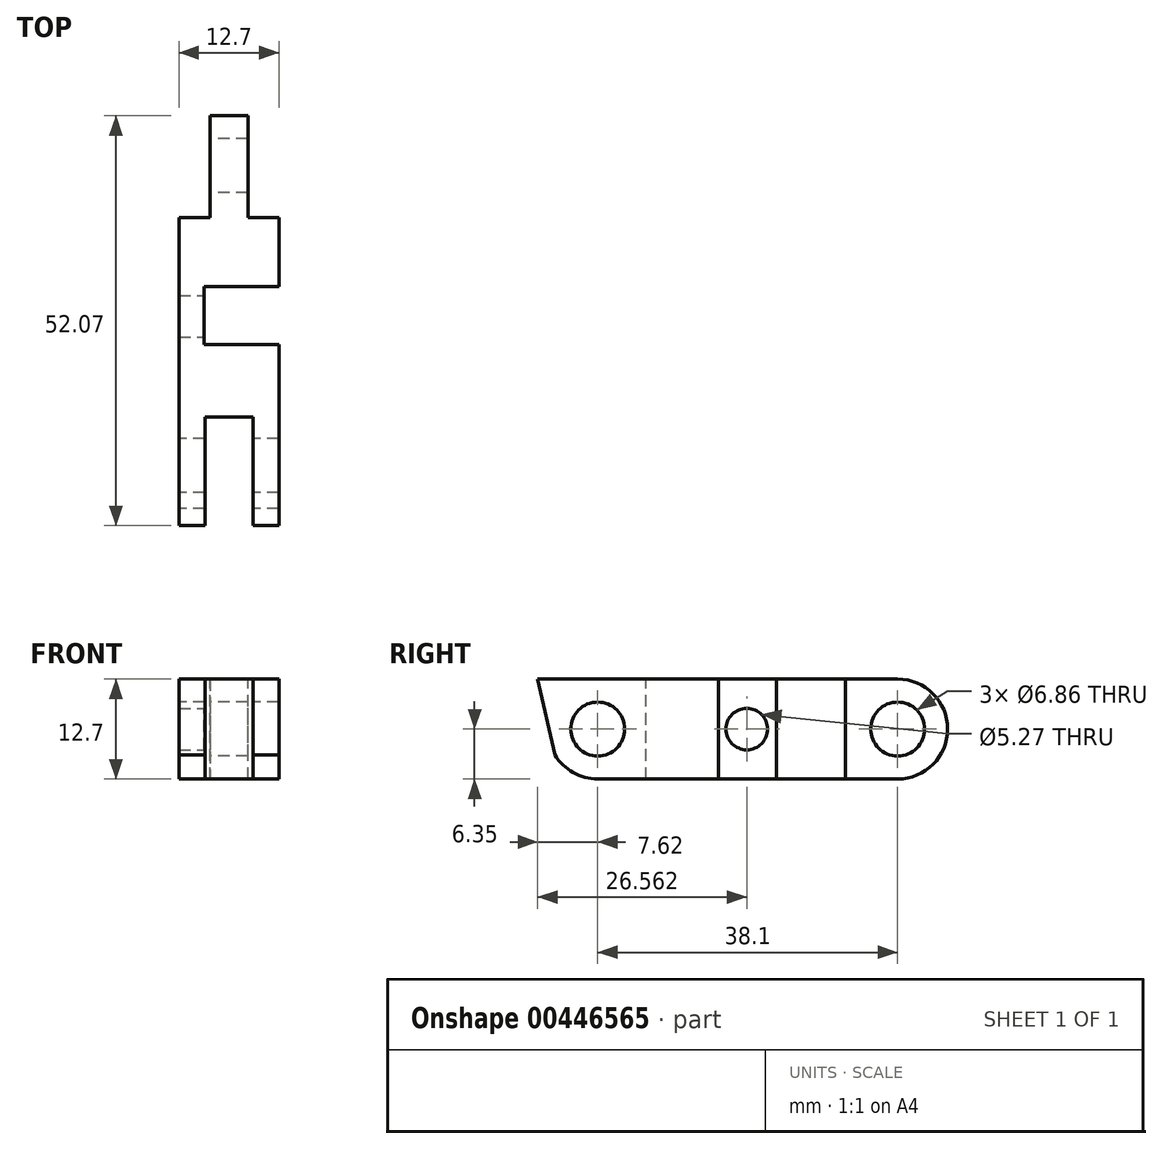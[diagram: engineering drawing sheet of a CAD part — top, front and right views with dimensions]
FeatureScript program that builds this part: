
annotation { "Feature Type Name" : "Feature", "Feature Type Description" : "" }
export const myFeature = defineFeature(function(context is Context, id is Id, definition is map)
    precondition{}
    {
        {
            var Q0;
            Q0=qCreatedBy(makeId("Right.planeOp"),FACE);
            var sketch = newSketch(context, id + "F0", { "sketchPlane" : qUnion([Q0])});
            skLineSegment(sketch, "E0.bottom", {"start": v(6.35, 0) * mm, "end": v(44.45, 0) * mm});
            skLineSegment(sketch, "E0.top", {"start": v(0, 12.7) * mm, "end": v(44.45, 12.7) * mm});
            skLineSegment(sketch, "E0.right", {"start": v(50.8, 6.35) * mm, "end": v(50.8, 6.35) * mm});
            skPoint(sketch, "E1.visualSharp", {"position": v(0, 0) * mm});
            skPoint(sketch, "E2.visualSharp", {"position": v(50.8, 0) * mm});
            skArc(sketch, "E2.filletArc", {"start": v(44.45, 0) * mm, "mid": v(48.94, 1.86) * mm, "end": v(50.8, 6.35) * mm});
            skPoint(sketch, "E3.visualSharp", {"position": v(50.8, 12.7) * mm});
            skArc(sketch, "E3.filletArc", {"start": v(50.8, 6.35) * mm, "mid": v(48.94, 10.84) * mm, "end": v(44.45, 12.7) * mm});
            skCircle(sketch, "E4", {"center": v(44.45, 6.35) * mm, "radius": 3.43 * mm});
            skCircle(sketch, "E5", {"center": v(6.35, 6.35) * mm, "radius": 3.43 * mm});
            skLineSegment(sketch, "E6", {"start": v(0, 12.7) * mm, "end": v(-1.27, 12.7) * mm});
            skArc(sketch, "E7", {"start": v(6.35, 0) * mm, "mid": v(3.23, 0.82) * mm, "end": v(0.91, 3.07) * mm});
            skLineSegment(sketch, "E8", {"start": v(-1.27, 12.7) * mm, "end": v(0.91, 3.07) * mm});
            skSolve(sketch);
        }
        {
            var Q0;
            Q0 = qSketchRegion(id + "F0", true);
            extrude(context, id + "F1", {"entities" : qUnion([Q0]), "depth" : 12.7 * mm});
        }
        {
            var Q0;
            Q0=makeQuery(id+"F1.opExtrude","SWEPT_FACE",FACE,{"disambiguationData":[OSD([sQuery(id+"F0.wireOp",EDGE,"E0.top")])]});
            var sketch = newSketch(context, id + "F2", { "sketchPlane" : qUnion([Q0])});
            skLineSegment(sketch, "E9.bottom", {"start": v(9.4, -9.23) * mm, "end": v(3.3, -9.23) * mm});
            skLineSegment(sketch, "E9.top", {"start": v(9.4, 12.5) * mm, "end": v(3.3, 12.5) * mm});
            skLineSegment(sketch, "E9.left", {"start": v(9.4, -9.23) * mm, "end": v(9.4, 12.5) * mm});
            skLineSegment(sketch, "E9.right", {"start": v(3.3, -9.23) * mm, "end": v(3.3, 12.5) * mm});
            skLineSegment(sketch, "E10.bottom", {"start": v(0, 51.09) * mm, "end": v(3.94, 51.09) * mm});
            skLineSegment(sketch, "E10.top", {"start": v(0, 37.85) * mm, "end": v(3.94, 37.85) * mm});
            skLineSegment(sketch, "E10.left", {"start": v(0, 51.09) * mm, "end": v(0, 37.85) * mm});
            skLineSegment(sketch, "E10.right", {"start": v(3.94, 51.09) * mm, "end": v(3.94, 37.85) * mm});
            skLineSegment(sketch, "E11.bottom", {"start": v(12.7, 37.85) * mm, "end": v(8.76, 37.85) * mm});
            skLineSegment(sketch, "E11.top", {"start": v(12.7, 51.09) * mm, "end": v(8.76, 51.09) * mm});
            skLineSegment(sketch, "E11.left", {"start": v(12.7, 37.85) * mm, "end": v(12.7, 51.09) * mm});
            skLineSegment(sketch, "E11.right", {"start": v(8.76, 37.85) * mm, "end": v(8.76, 51.09) * mm});
            skSolve(sketch);
        }
        {
            var Q0;
            Q0 = qSketchRegion(id + "F2", true);
            extrude(context, id + "F3", {"entities" : qUnion([Q0]), "operationType" : NewBodyOperationType.REMOVE, "oppositeDirection" : true, "depth" : 25.4 * mm});
        }
        {
            var Q0;
            Q0=makeQuery(id+"F1.opExtrude","CAP_FACE",FACE,{"disambiguationData":[OSD([sQuery(id+"F0.wireOp",EDGE,"E0.bottom"),sQuery(id+"F0.wireOp",EDGE,"E0.top"),sQuery(id+"F0.wireOp",EDGE,"E0.left"),sQuery(id+"F0.wireOp",EDGE,"E1.filletArc"),sQuery(id+"F0.wireOp",EDGE,"E2.filletArc"),sQuery(id+"F0.wireOp",EDGE,"E3.filletArc"),sQuery(id+"F0.wireOp",EDGE,"E4"),sQuery(id+"F0.wireOp",EDGE,"E5")])],"isStart":false});
            var sketch = newSketch(context, id + "F4", { "sketchPlane" : qUnion([Q0])});
            skLineSegment(sketch, "E12.bottom", {"start": v(21.72, 12.7) * mm, "end": v(29.08, 12.7) * mm});
            skLineSegment(sketch, "E12.top", {"start": v(21.72, 0) * mm, "end": v(29.08, 0) * mm});
            skLineSegment(sketch, "E12.left", {"start": v(21.72, 12.7) * mm, "end": v(21.72, 0) * mm});
            skLineSegment(sketch, "E12.right", {"start": v(29.08, 12.7) * mm, "end": v(29.08, 0) * mm});
            skSolve(sketch);
        }
        {
            var Q0;
            Q0 = qSketchRegion(id + "F4", true);
            extrude(context, id + "F5", {"entities" : qUnion([Q0]), "operationType" : NewBodyOperationType.REMOVE, "oppositeDirection" : true, "depth" : 9.52 * mm});
        }
        {
            var Q0;
            Q0=makeQuery(id+"F5.boolean.opBoolean","COPY",FACE,{"derivedFrom":makeQuery(id+"F5.opExtrude","CAP_FACE",FACE,{"disambiguationData":[OSD([sQuery(id+"F4.wireOp",EDGE,"E12.bottom"),sQuery(id+"F4.wireOp",EDGE,"E12.top"),sQuery(id+"F4.wireOp",EDGE,"E12.left"),sQuery(id+"F4.wireOp",EDGE,"E12.right")])],"isStart":false})});
            var sketch = newSketch(context, id + "F6", { "sketchPlane" : qUnion([Q0])});
            skCircle(sketch, "E13", {"center": v(25.3, 6.35) * mm, "radius": 2.64 * mm});
            skSolve(sketch);
        }
        {
            var Q0;
            Q0 = qSketchRegion(id + "F6", true);
            extrude(context, id + "F7", {"entities" : qUnion([Q0]), "operationType" : NewBodyOperationType.REMOVE, "oppositeDirection" : true, "depth" : 25.4 * mm});
        }
    });
